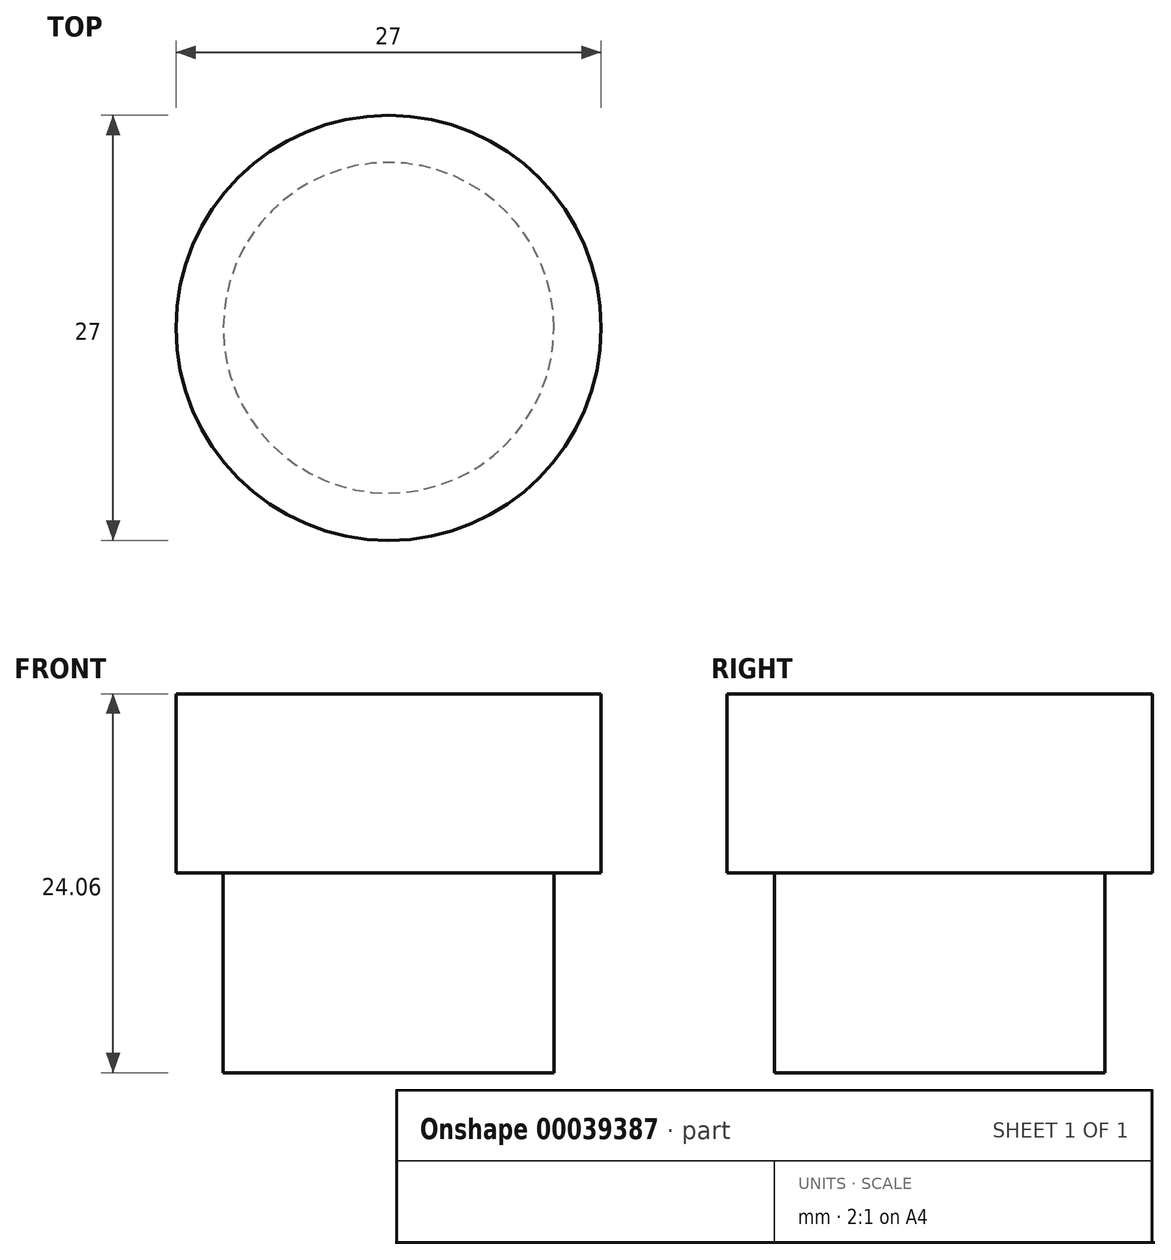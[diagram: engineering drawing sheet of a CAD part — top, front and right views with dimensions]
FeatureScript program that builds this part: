
annotation { "Feature Type Name" : "Feature", "Feature Type Description" : "" }
export const myFeature = defineFeature(function(context is Context, id is Id, definition is map)
    precondition{}
    {
        {
            var Q0;
            Q0=qCreatedBy(makeId("Top.planeOp"),FACE);
            var sketch = newSketch(context, id + "F0", { "sketchPlane" : qUnion([Q0])});
            skCircle(sketch, "E0", {"center": v(0, 0) * mm, "radius": 10.5 * mm});
            skLineSegment(sketch, "E1", {"start": v(0, 0) * mm, "end": v(10.5, 0) * mm});
            skSolve(sketch);
        }
        {
            var Q0;
            Q0 = qSketchRegion(id + "F0", true);
            extrude(context, id + "F1", {"entities" : qUnion([Q0]), "depth" : 12.7 * mm});
        }
        {
            var Q0;
            Q0=makeQuery(id+"F1.opExtrude","CAP_FACE",FACE,{"disambiguationData":[OSD([sQuery(id+"F0.wireOp",EDGE,"E0")])],"isStart":false});
            var sketch = newSketch(context, id + "F2", { "sketchPlane" : qUnion([Q0])});
            skCircle(sketch, "E2", {"center": v(0, 0) * mm, "radius": 13.5 * mm});
            skLineSegment(sketch, "E3", {"start": v(0, 0) * mm, "end": v(13.5, 0) * mm});
            skSolve(sketch);
        }
        {
            var Q0;
            Q0 = qSketchRegion(id + "F2", true);
            extrude(context, id + "F3", {"entities" : qUnion([Q0]), "operationType" : NewBodyOperationType.ADD, "depth" : 11.36 * mm});
        }
    });
